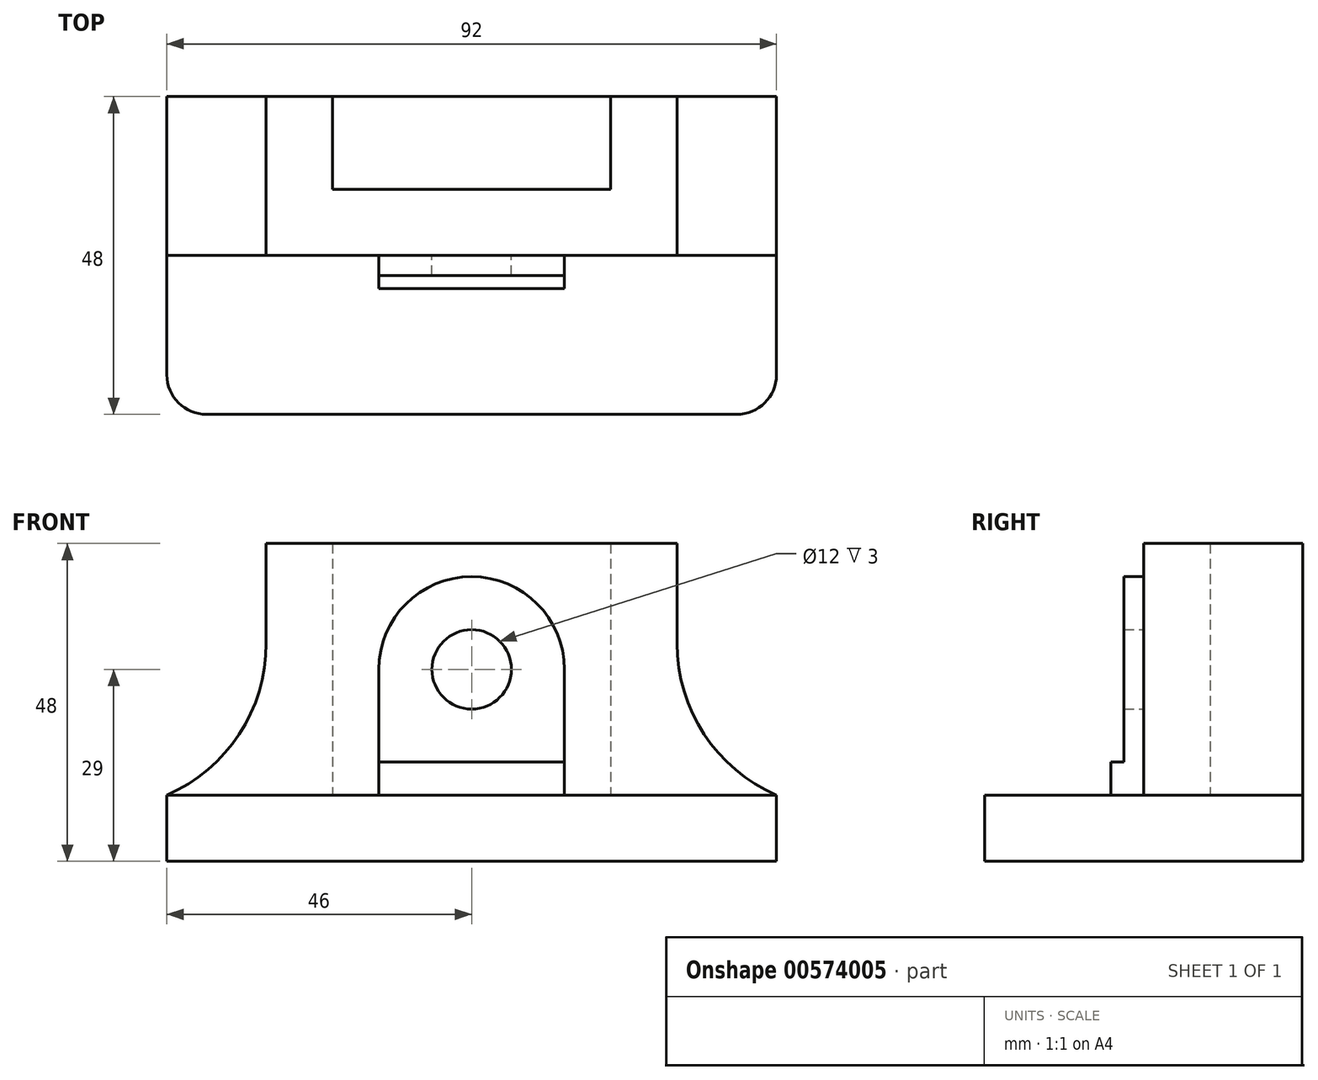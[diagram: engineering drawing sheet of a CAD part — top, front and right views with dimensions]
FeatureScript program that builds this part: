
annotation { "Feature Type Name" : "Feature", "Feature Type Description" : "" }
export const myFeature = defineFeature(function(context is Context, id is Id, definition is map)
    precondition{}
    {
        {
            var Q0;
            Q0=qCreatedBy(makeId("Top.planeOp"),FACE);
            var sketch = newSketch(context, id + "F0", { "sketchPlane" : qUnion([Q0])});
            skLineSegment(sketch, "E0.bottom", {"start": v(46, -24) * mm, "end": v(-46, -24) * mm});
            skLineSegment(sketch, "E0.top", {"start": v(46, 24) * mm, "end": v(-46, 24) * mm});
            skLineSegment(sketch, "E0.left", {"start": v(46, -24) * mm, "end": v(46, 24) * mm});
            skLineSegment(sketch, "E0.right", {"start": v(-46, -24) * mm, "end": v(-46, 24) * mm});
            skPoint(sketch, "E0.middle", {"position": v(0, 0) * mm});
            skLineSegment(sketch, "E1", {"start": v(-31, 24) * mm, "end": v(-31, 0) * mm});
            skLineSegment(sketch, "E2", {"start": v(-31, 0) * mm, "end": v(31, 0) * mm});
            skLineSegment(sketch, "E3", {"start": v(31, 0) * mm, "end": v(31, 24) * mm});
            skLineSegment(sketch, "E4", {"start": v(31, 24) * mm, "end": v(21, 24) * mm});
            skLineSegment(sketch, "E5", {"start": v(21, 24) * mm, "end": v(21, 10) * mm});
            skLineSegment(sketch, "E6", {"start": v(21, 10) * mm, "end": v(-21, 10) * mm});
            skLineSegment(sketch, "E7", {"start": v(-21, 10) * mm, "end": v(-21, 24) * mm});
            skLineSegment(sketch, "E8", {"start": v(-21, 24) * mm, "end": v(-31, 24) * mm});
            skSolve(sketch);
        }
        {
            var Q0;
            Q0=makeQuery(id+"F0.imprint","IMPRINT",FACE,{"disambiguationData":[TD([[makeQuery(id+"F0.imprint","IMPRINT",EDGE,{"derivedFrom":sQuery(id+"F0.wireOp",EDGE,"E1")}),1.0]])]});
            extrude(context, id + "F1", {"entities" : qUnion([Q0]), "depth" : 48 * mm, "offsetDistance" : 25 * mm});
        }
        {
            var Q0;
            Q0 = qSketchRegion(id + "F0", true);
            extrude(context, id + "F2", {"entities" : qUnion([Q0]), "operationType" : NewBodyOperationType.ADD, "depth" : 10 * mm, "offsetDistance" : 25 * mm});
        }
        {
            var Q0;
            Q0=makeQuery(id+"F2.boolean.opBoolean","INTERSECT",EDGE,{"derivedFrom":[makeQuery(id+"F1.opExtrude","SWEPT_FACE",FACE,{"disambiguationData":[OSD([sQuery(id+"F0.wireOp",EDGE,"E3")])]}),makeQuery(id+"F2.opExtrude","CAP_FACE",FACE,{"disambiguationData":[OSD([sQuery(id+"F0.wireOp",EDGE,"E0.bottom"),sQuery(id+"F0.wireOp",EDGE,"E0.top"),sQuery(id+"F0.wireOp",EDGE,"E0.left"),sQuery(id+"F0.wireOp",EDGE,"E0.right"),sQuery(id+"F0.wireOp",EDGE,"E4"),sQuery(id+"F0.wireOp",EDGE,"E8")])],"isStart":false})]});
            fillet(context, id + "F3", {"entities" : qUnion([Q0]), "radius" : 25 * mm, "tangentPropagation" : true, "allowEdgeOverflow" : false});
        }
        {
            var Q0;
            Q0=makeQuery(id+"F2.boolean.opBoolean","INTERSECT",EDGE,{"derivedFrom":[makeQuery(id+"F1.opExtrude","SWEPT_FACE",FACE,{"disambiguationData":[OSD([sQuery(id+"F0.wireOp",EDGE,"E1")])]}),makeQuery(id+"F2.opExtrude","CAP_FACE",FACE,{"disambiguationData":[OSD([sQuery(id+"F0.wireOp",EDGE,"E0.bottom"),sQuery(id+"F0.wireOp",EDGE,"E0.top"),sQuery(id+"F0.wireOp",EDGE,"E0.left"),sQuery(id+"F0.wireOp",EDGE,"E0.right"),sQuery(id+"F0.wireOp",EDGE,"E4"),sQuery(id+"F0.wireOp",EDGE,"E8")])],"isStart":false})]});
            fillet(context, id + "F4", {"entities" : qUnion([Q0]), "radius" : 25 * mm, "tangentPropagation" : true, "allowEdgeOverflow" : false});
        }
        {
            var Q0;
            Q0=makeQuery(id+"F1.opExtrude","SWEPT_FACE",FACE,{"disambiguationData":[OSD([sQuery(id+"F0.wireOp",EDGE,"E2")])]});
            var sketch = newSketch(context, id + "F5", { "sketchPlane" : qUnion([Q0])});
            skArc(sketch, "E9", {"start": v(14, 29) * mm, "mid": v(0, 43) * mm, "end": v(-14, 29) * mm});
            skCircle(sketch, "E10", {"center": v(0, 29) * mm, "radius": 6 * mm});
            skLineSegment(sketch, "E11", {"start": v(14, 29) * mm, "end": v(14, 10) * mm});
            skLineSegment(sketch, "E12", {"start": v(-14, 29) * mm, "end": v(-14, 10) * mm});
            skLineSegment(sketch, "E13", {"start": v(-14, 10) * mm, "end": v(14, 10) * mm});
            skLineSegment(sketch, "E14.bottom", {"start": v(-14, 15) * mm, "end": v(14, 15) * mm});
            skLineSegment(sketch, "E14.left", {"start": v(-14, 15) * mm, "end": v(-14, 10) * mm});
            skLineSegment(sketch, "E14.right", {"start": v(14, 15) * mm, "end": v(14, 10) * mm});
            skSolve(sketch);
        }
        {
            var Q0;
            Q0=makeQuery(id+"F5.imprint","IMPRINT",FACE,{"disambiguationData":[TD([[makeQuery(id+"F5.imprint","IMPRINT",EDGE,{"derivedFrom":sQuery(id+"F5.wireOp",EDGE,"E9")}),1.0]])]});
            extrude(context, id + "F6", {"entities" : qUnion([Q0]), "operationType" : NewBodyOperationType.ADD, "depth" : 3 * mm, "offsetDistance" : 25 * mm});
        }
        {
            var Q0;
            Q0 = qSketchRegion(id + "F5", true);
            extrude(context, id + "F7", {"entities" : qUnion([Q0]), "operationType" : NewBodyOperationType.ADD, "depth" : 3 * mm, "offsetDistance" : 25 * mm});
        }
        {
            var Q0;
            Q0=makeQuery(id+"F2.opExtrude","SWEPT_EDGE",EDGE,{"disambiguationData":[OSD([sQuery(id+"F0.wireOp",EDGE,"E0.bottom"),sQuery(id+"F0.wireOp",EDGE,"E0.left")])]});
            fillet(context, id + "F8", {"entities" : qUnion([Q0]), "radius" : 6 * mm, "tangentPropagation" : true, "allowEdgeOverflow" : false});
        }
        {
            var Q0;
            Q0=makeQuery(id+"F2.opExtrude","SWEPT_EDGE",EDGE,{"disambiguationData":[OSD([sQuery(id+"F0.wireOp",EDGE,"E0.bottom"),sQuery(id+"F0.wireOp",EDGE,"E0.right")])]});
            fillet(context, id + "F9", {"entities" : qUnion([Q0]), "radius" : 6 * mm, "tangentPropagation" : true, "allowEdgeOverflow" : false});
        }
        {
            var Q0;
            {var subQ2=sQuery(id+"F0.wireOp",EDGE,"E1");var subQ8=sQuery(id+"F0.wireOp",EDGE,"E2");Q0=makeQuery(id+"F6.boolean.opBoolean","SPLIT",FACE,{"disambiguationData":[TD([makeQuery(id+"F1.opExtrude","SWEPT_FACE",FACE,{"disambiguationData":[OSD([subQ2])]})])],"derivedFrom":makeQuery(id+"F1.opExtrude","SWEPT_FACE",FACE,{"disambiguationData":[OSD([subQ8])]})});}
            var sketch = newSketch(context, id + "F10", { "sketchPlane" : qUnion([Q0])});
            skLineSegment(sketch, "E15.bottom", {"start": v(-14, 15) * mm, "end": v(14, 15) * mm});
            skLineSegment(sketch, "E15.top", {"start": v(-14, 10) * mm, "end": v(14, 10) * mm});
            skLineSegment(sketch, "E15.left", {"start": v(-14, 15) * mm, "end": v(-14, 10) * mm});
            skLineSegment(sketch, "E15.right", {"start": v(14, 15) * mm, "end": v(14, 10) * mm});
            skSolve(sketch);
        }
        {
            var Q0;
            Q0 = qSketchRegion(id + "F10", true);
            extrude(context, id + "F11", {"entities" : qUnion([Q0]), "operationType" : NewBodyOperationType.ADD, "depth" : 5 * mm, "offsetDistance" : 25 * mm});
        }
    });
